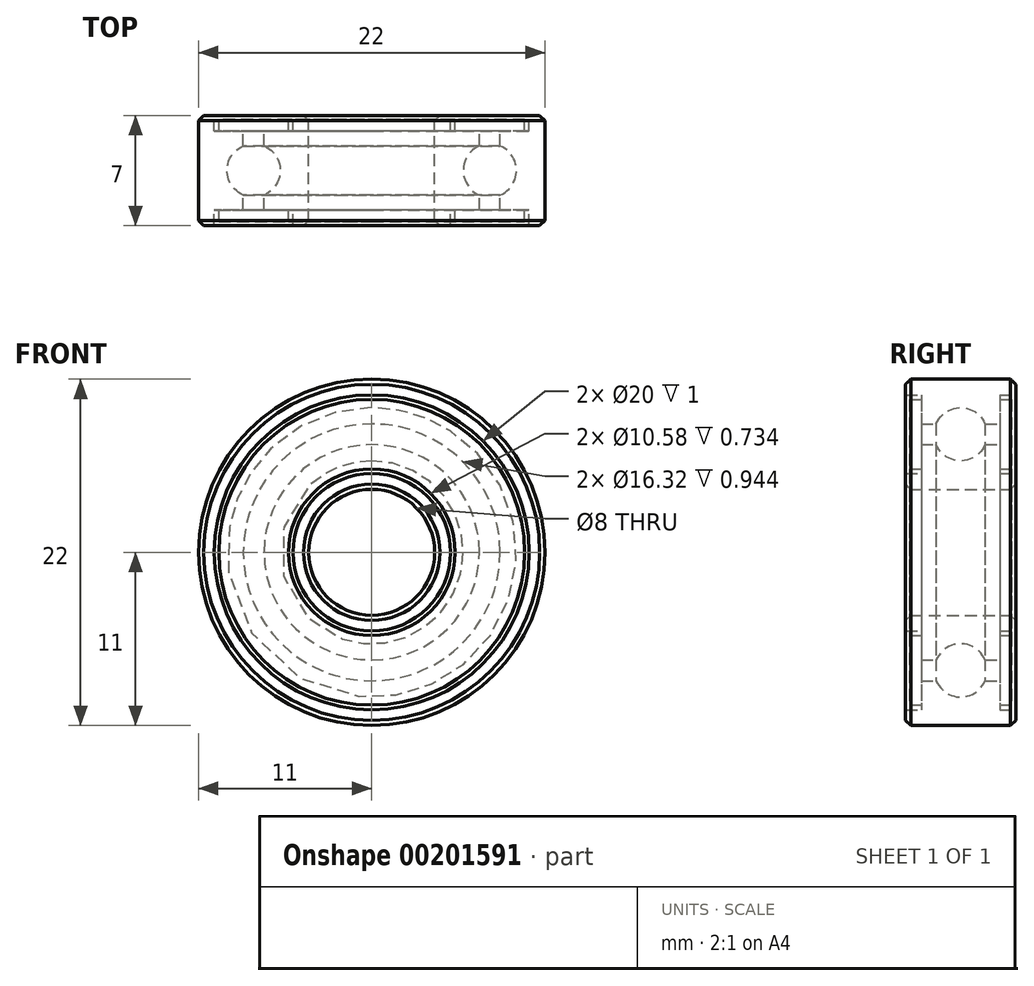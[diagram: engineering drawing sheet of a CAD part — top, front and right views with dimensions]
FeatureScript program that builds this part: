
annotation { "Feature Type Name" : "Feature", "Feature Type Description" : "" }
export const myFeature = defineFeature(function(context is Context, id is Id, definition is map)
    precondition{}
    {
        {
            var Q0;
            Q0=qCreatedBy(makeId("Front.planeOp"),FACE);
            var sketch = newSketch(context, id + "F0", { "sketchPlane" : qUnion([Q0])});
            skCircle(sketch, "E0.0", {"center": v(0, 0) * mm, "radius": 11 * mm});
            skCircle(sketch, "E0.1", {"center": v(0, 0) * mm, "radius": 6.84 * mm});
            skCircle(sketch, "E0.2", {"center": v(0, 0) * mm, "radius": 8.16 * mm});
            skCircle(sketch, "E0.3", {"center": v(0, 0) * mm, "radius": 4 * mm});
            skSolve(sketch);
        }
        {
            var Q0;
            Q0=qCreatedBy(makeId("Right.planeOp"),FACE);
            var sketch = newSketch(context, id + "F1", { "sketchPlane" : qUnion([Q0])});
            skLineSegment(sketch, "E1.0.0", {"start": v(3.5, 11) * mm, "end": v(0, 11) * mm});
            skArc(sketch, "E1.0.4", {"start": v(0, 9.19) * mm, "mid": v(0.93, 8.9) * mm, "end": v(1.56, 8.16) * mm});
            skLineSegment(sketch, "E1.0.5", {"start": v(1.56, 8.16) * mm, "end": v(3.5, 8.16) * mm});
            skLineSegment(sketch, "E1.0.6", {"start": v(3.5, 8.16) * mm, "end": v(3.5, 11) * mm});
            skLineSegment(sketch, "E1.1.3", {"start": v(0, 4) * mm, "end": v(3.5, 4) * mm});
            skLineSegment(sketch, "E1.1.5", {"start": v(3.5, 4) * mm, "end": v(3.5, 6.84) * mm});
            skLineSegment(sketch, "E1.1.6", {"start": v(3.5, 6.84) * mm, "end": v(1.56, 6.84) * mm});
            skArc(sketch, "E1.1.7", {"start": v(1.56, 6.84) * mm, "mid": v(0.93, 6.1) * mm, "end": v(0, 5.81) * mm});
            skLineSegment(sketch, "E2", {"start": v(-5.57, 7.5) * mm, "end": v(5.65, 7.5) * mm, "construction": true});
            skLineSegment(sketch, "E3", {"start": v(0, 11) * mm, "end": v(0, 9.19) * mm});
            skLineSegment(sketch, "E4", {"start": v(0, 5.81) * mm, "end": v(0, 4) * mm});
            skLineSegment(sketch, "E5", {"start": v(0, 12.74) * mm, "end": v(0, 2.66) * mm, "construction": true});
            skLineSegment(sketch, "E6.rect.bottom", {"start": v(3.5, 5) * mm, "end": v(2.5, 5) * mm});
            skLineSegment(sketch, "E6.rect.top", {"start": v(3.5, 10) * mm, "end": v(2.5, 10) * mm});
            skLineSegment(sketch, "E6.rect.right", {"start": v(2.5, 5) * mm, "end": v(2.5, 10) * mm});
            skPoint(sketch, "E6.rect.middle", {"position": v(3.5, 7.5) * mm});
            skLineSegment(sketch, "E7.MirrorCS", {"start": v(-1.56, 8.16) * mm, "end": v(-3.5, 8.16) * mm});
            skLineSegment(sketch, "E8.MirrorCS", {"start": v(0, 4) * mm, "end": v(-3.5, 4) * mm});
            skArc(sketch, "E9.MirrorCS", {"start": v(-1.56, 6.84) * mm, "mid": v(-0.93, 6.1) * mm, "end": v(0, 5.81) * mm});
            skLineSegment(sketch, "E10.MirrorCS", {"start": v(-3.5, 6.84) * mm, "end": v(-1.56, 6.84) * mm});
            skArc(sketch, "E11.MirrorCS", {"start": v(0, 9.19) * mm, "mid": v(-0.93, 8.9) * mm, "end": v(-1.56, 8.16) * mm});
            skLineSegment(sketch, "E12.MirrorCS", {"start": v(-3.5, 8.16) * mm, "end": v(-3.5, 11) * mm});
            skLineSegment(sketch, "E13.MirrorCS", {"start": v(-3.5, 4) * mm, "end": v(-3.5, 6.84) * mm});
            skLineSegment(sketch, "E14.MirrorCS", {"start": v(-3.5, 11) * mm, "end": v(0, 11) * mm});
            skLineSegment(sketch, "E15", {"start": v(3.23, 10) * mm, "end": v(3.23, 5) * mm});
            skLineSegment(sketch, "E16", {"start": v(2.5, 9.7) * mm, "end": v(3.5, 9.7) * mm});
            skLineSegment(sketch, "E17.MirrorCS", {"start": v(2.5, 5.3) * mm, "end": v(3.5, 5.3) * mm});
            skLineSegment(sketch, "E18.MirrorCS", {"start": v(-2.5, 9.7) * mm, "end": v(-3.5, 9.7) * mm});
            skLineSegment(sketch, "E19.MirrorCS", {"start": v(-2.5, 5.3) * mm, "end": v(-3.5, 5.3) * mm});
            skLineSegment(sketch, "E20.MirrorCS", {"start": v(-3.23, 10) * mm, "end": v(-3.23, 5) * mm});
            skLineSegment(sketch, "E21.MirrorCS", {"start": v(-3.5, 10) * mm, "end": v(-2.5, 10) * mm});
            skLineSegment(sketch, "E22.MirrorCS", {"start": v(-2.5, 5) * mm, "end": v(-2.5, 10) * mm});
            skLineSegment(sketch, "E23.MirrorCS", {"start": v(-3.5, 5) * mm, "end": v(-2.5, 5) * mm});
            skSolve(sketch);
        }
        {
            var Q0;
            {var subQ7=sQuery(id+"F1.wireOp",EDGE,"E1.0.0");Q0=makeQuery(id+"F1.imprint","IMPRINT",FACE,{"disambiguationData":[TD([[makeQuery(id+"F1.imprint","IMPRINT",EDGE,{"derivedFrom":subQ7}),1.0]])]});}
            var Q1;
            {var subQ8=sQuery(id+"F1.wireOp",EDGE,"E1.1.3");Q1=makeQuery(id+"F1.imprint","IMPRINT",FACE,{"disambiguationData":[TD([[makeQuery(id+"F1.imprint","IMPRINT",EDGE,{"derivedFrom":subQ8}),1.0]])]});}
            var Q2;
            Q2=makeQuery(id+"F1.imprint","IMPRINT",FACE,{"disambiguationData":[TD([[makeQuery(id+"F1.imprint","IMPRINT",EDGE,{"derivedFrom":sQuery(id+"F1.wireOp",EDGE,"E4")}),-1.0]])]});
            var Q3;
            Q3=makeQuery(id+"F1.imprint","IMPRINT",FACE,{"disambiguationData":[TD([[makeQuery(id+"F1.imprint","IMPRINT",EDGE,{"derivedFrom":sQuery(id+"F1.wireOp",EDGE,"E3")}),-1.0]])]});
            var Q4;
            {var subQ0=sQuery(id+"F1.wireOp",EDGE,"E15");var subQ3=sQuery(id+"F1.wireOp",EDGE,"E1.0.5");var subQ4=makeQuery(id+"F1.imprint","INTERSECT",VERTEX,{"derivedFrom":[subQ3,subQ0]});Q4=makeQuery(id+"F1.imprint","IMPRINT",FACE,{"disambiguationData":[TD([[makeQuery(id+"F1.imprint","IMPRINT",EDGE,{"disambiguationData":[TD([[subQ4,1.0]])],"derivedFrom":subQ3}),1.0]])]});}
            var Q5;
            {var subQ0=sQuery(id+"F1.wireOp",EDGE,"E15");var subQ3=sQuery(id+"F1.wireOp",EDGE,"E1.0.5");var subQ4=makeQuery(id+"F1.imprint","INTERSECT",VERTEX,{"derivedFrom":[subQ3,subQ0]});Q5=makeQuery(id+"F1.imprint","IMPRINT",FACE,{"disambiguationData":[TD([[makeQuery(id+"F1.imprint","IMPRINT",EDGE,{"disambiguationData":[TD([[subQ4,1.0]])],"derivedFrom":subQ3}),-1.0]])]});}
            var Q6;
            {var subQ1=sQuery(id+"F1.wireOp",EDGE,"E15");var subQ5=sQuery(id+"F1.wireOp",EDGE,"E1.1.6");var subQ6=makeQuery(id+"F1.imprint","INTERSECT",VERTEX,{"derivedFrom":[subQ5,subQ1]});Q6=makeQuery(id+"F1.imprint","IMPRINT",FACE,{"disambiguationData":[TD([[makeQuery(id+"F1.imprint","IMPRINT",EDGE,{"disambiguationData":[TD([[subQ6,-1.0]])],"derivedFrom":subQ5}),1.0]])]});}
            var Q7;
            {var subQ1=sQuery(id+"F1.wireOp",EDGE,"E7.MirrorCS");var subQ5=sQuery(id+"F1.wireOp",EDGE,"E20.MirrorCS");var subQ7=makeQuery(id+"F1.imprint","INTERSECT",VERTEX,{"derivedFrom":[subQ1,subQ5]});Q7=makeQuery(id+"F1.imprint","IMPRINT",FACE,{"disambiguationData":[TD([[makeQuery(id+"F1.imprint","IMPRINT",EDGE,{"disambiguationData":[TD([[subQ7,1.0]])],"derivedFrom":subQ1}),-1.0]])]});}
            var Q8;
            {var subQ1=sQuery(id+"F1.wireOp",EDGE,"E10.MirrorCS");var subQ5=sQuery(id+"F1.wireOp",EDGE,"E20.MirrorCS");var subQ7=makeQuery(id+"F1.imprint","INTERSECT",VERTEX,{"derivedFrom":[subQ1,subQ5]});Q8=makeQuery(id+"F1.imprint","IMPRINT",FACE,{"disambiguationData":[TD([[makeQuery(id+"F1.imprint","IMPRINT",EDGE,{"disambiguationData":[TD([[subQ7,-1.0]])],"derivedFrom":subQ1}),-1.0]])]});}
            var Q9;
            {var subQ3=sQuery(id+"F1.wireOp",EDGE,"E7.MirrorCS");var subQ5=sQuery(id+"F1.wireOp",EDGE,"E20.MirrorCS");var subQ7=makeQuery(id+"F1.imprint","INTERSECT",VERTEX,{"derivedFrom":[subQ3,subQ5]});Q9=makeQuery(id+"F1.imprint","IMPRINT",FACE,{"disambiguationData":[TD([[makeQuery(id+"F1.imprint","IMPRINT",EDGE,{"disambiguationData":[TD([[subQ7,1.0]])],"derivedFrom":subQ3}),1.0]])]});}
            var Q10;
            Q10=sQuery(id+"F0.wireOp",EDGE,"E0.0");
            revolve(context, id + "F2", {"entities" : qUnion([Q0, Q1, Q2, Q3, Q4, Q5, Q6, Q7, Q8, Q9]), "axis" : qUnion([Q10]), "revolveType" : RevolveType.FULL});
        }
        {
            var Q0;
            Q0=makeQuery(id+"F2.opRevolve","SWEPT_FACE",FACE,{"disambiguationData":[OSD([sQuery(id+"F1.wireOp",EDGE,"E1.1.3"),sQuery(id+"F1.wireOp",EDGE,"E8.MirrorCS")])]});
            var Q1;
            Q1=makeQuery(id+"F2.opRevolve","SWEPT_FACE",FACE,{"disambiguationData":[OSD([sQuery(id+"F1.wireOp",EDGE,"E1.0.0"),sQuery(id+"F1.wireOp",EDGE,"E14.MirrorCS")])]});
            chamfer(context, id + "F3", {"entities" : qUnion([Q0, Q1]), "width" : .33 * mm, "tangentPropagation" : true});
        }
        {
            var Q0;
            Q0=makeQuery(id+"F2.opRevolve","SWEPT_BODY",BODY,{"disambiguationData":[OSD([sQuery(id+"F1.wireOp",EDGE,"E1.0.0"),sQuery(id+"F1.wireOp",EDGE,"E1.0.4"),sQuery(id+"F1.wireOp",EDGE,"E1.0.5"),sQuery(id+"F1.wireOp",EDGE,"E1.0.6"),sQuery(id+"F1.wireOp",EDGE,"E1.1.3"),sQuery(id+"F1.wireOp",EDGE,"E1.1.5"),sQuery(id+"F1.wireOp",EDGE,"E1.1.6"),sQuery(id+"F1.wireOp",EDGE,"E1.1.7"),sQuery(id+"F1.wireOp",EDGE,"E6.rect.bottom"),sQuery(id+"F1.wireOp",EDGE,"E6.rect.top"),sQuery(id+"F1.wireOp",EDGE,"E6.rect.right"),sQuery(id+"F1.wireOp",EDGE,"E7.MirrorCS"),sQuery(id+"F1.wireOp",EDGE,"E8.MirrorCS"),sQuery(id+"F1.wireOp",EDGE,"E9.MirrorCS"),sQuery(id+"F1.wireOp",EDGE,"E10.MirrorCS"),sQuery(id+"F1.wireOp",EDGE,"E11.MirrorCS"),sQuery(id+"F1.wireOp",EDGE,"E12.MirrorCS"),sQuery(id+"F1.wireOp",EDGE,"E13.MirrorCS"),sQuery(id+"F1.wireOp",EDGE,"E14.MirrorCS"),sQuery(id+"F1.wireOp",EDGE,"E15"),sQuery(id+"F1.wireOp",EDGE,"E16"),sQuery(id+"F1.wireOp",EDGE,"E17.MirrorCS"),sQuery(id+"F1.wireOp",EDGE,"E18.MirrorCS"),sQuery(id+"F1.wireOp",EDGE,"E19.MirrorCS"),sQuery(id+"F1.wireOp",EDGE,"E20.MirrorCS"),sQuery(id+"F1.wireOp",EDGE,"E21.MirrorCS"),sQuery(id+"F1.wireOp",EDGE,"E22.MirrorCS"),sQuery(id+"F1.wireOp",EDGE,"E23.MirrorCS")])]});
            transform(context, id + "F4", {"entities" : qUnion([Q0]), "transformType" : TransformType.TRANSLATION_3D, "dx" : 0 * mm, "dy" : 0 * mm, "dz" : 0 * mm, "makeCopy" : false});
        }
    });
